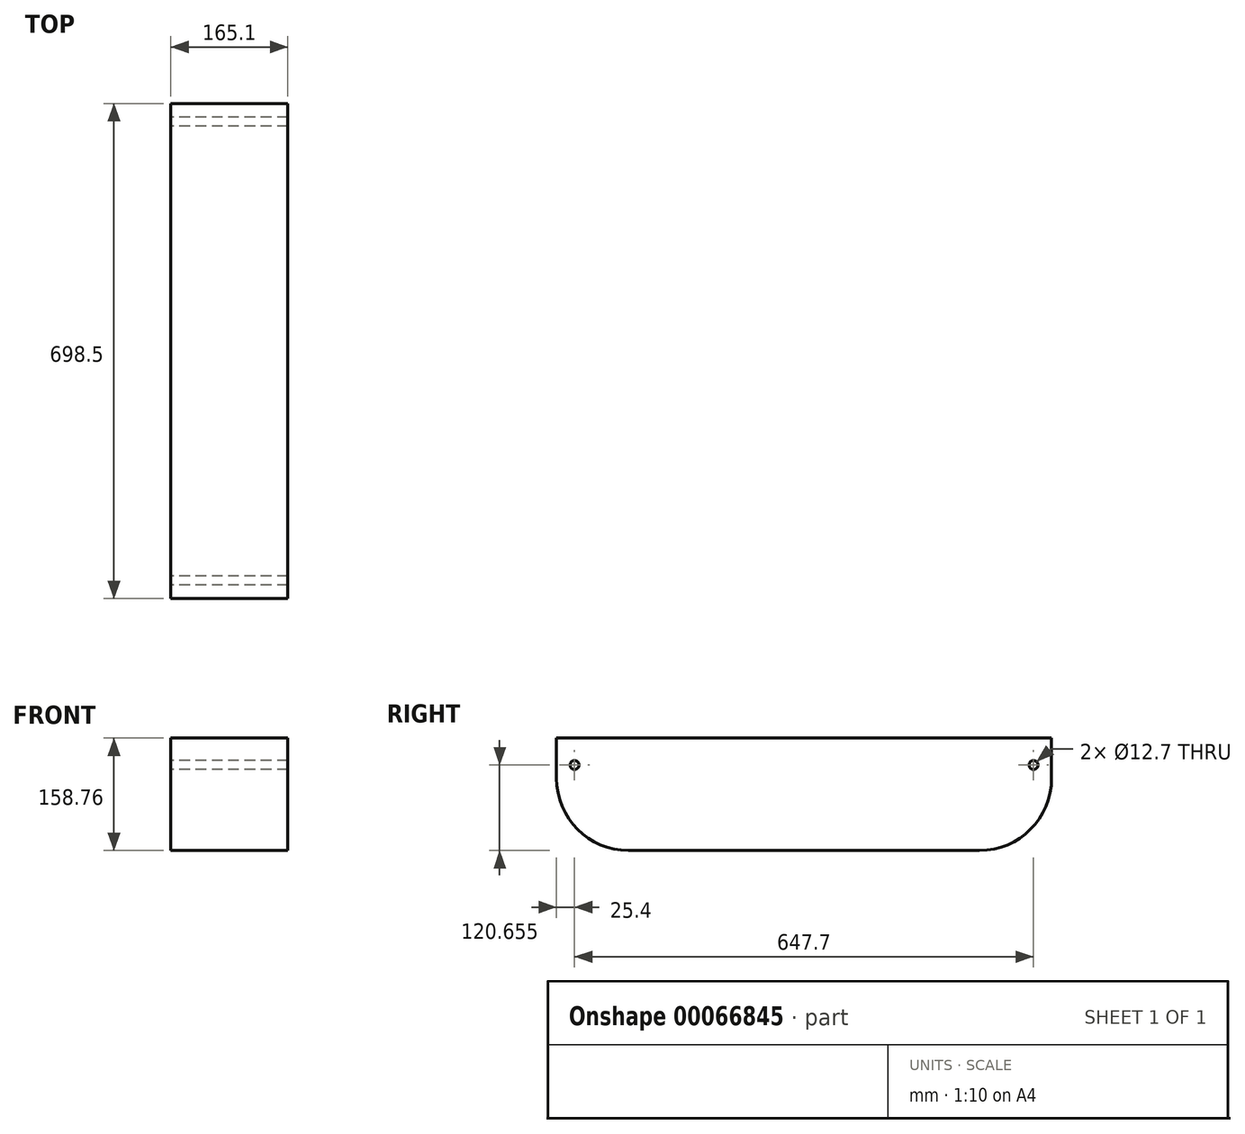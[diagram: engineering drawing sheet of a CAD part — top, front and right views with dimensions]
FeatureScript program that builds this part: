
annotation { "Feature Type Name" : "Feature", "Feature Type Description" : "" }
export const myFeature = defineFeature(function(context is Context, id is Id, definition is map)
    precondition{}
    {
        {
            var Q0;
            Q0=qCreatedBy(makeId("Right.planeOp"),FACE);
            var sketch = newSketch(context, id + "F0", { "sketchPlane" : qUnion([Q0])});
            skLineSegment(sketch, "E0.rect.bottom", {"start": v(349.25, 79.38) * mm, "end": v(-349.25, 79.38) * mm});
            skLineSegment(sketch, "E0.rect.top", {"start": v(349.25, -79.37) * mm, "end": v(-349.25, -79.37) * mm});
            skLineSegment(sketch, "E0.rect.left", {"start": v(349.25, 79.38) * mm, "end": v(349.25, -79.37) * mm});
            skLineSegment(sketch, "E0.rect.right", {"start": v(-349.25, 79.38) * mm, "end": v(-349.25, -79.37) * mm});
            skPoint(sketch, "E0.rect.middle", {"position": v(0, 0) * mm});
            skCircle(sketch, "E1", {"center": v(323.85, 41.27) * mm, "radius": 6.35 * mm});
            skCircle(sketch, "E2", {"center": v(-323.85, 41.27) * mm, "radius": 6.35 * mm});
            skSolve(sketch);
        }
        {
            var Q0;
            Q0=makeQuery(id+"F0.imprint","IMPRINT",FACE,{"disambiguationData":[TD([[makeQuery(id+"F0.imprint","IMPRINT",EDGE,{"derivedFrom":sQuery(id+"F0.wireOp",EDGE,"E0.rect.bottom")}),1.0]])]});
            extrude(context, id + "F1", {"entities" : qUnion([Q0]), "depth" : 165.1 * mm});
        }
        {
            var Q0;
            Q0=makeQuery(id+"F1.opExtrude","SWEPT_EDGE",EDGE,{"disambiguationData":[OSD([sQuery(id+"F0.wireOp",EDGE,"E0.rect.top"),sQuery(id+"F0.wireOp",EDGE,"E0.rect.left")])]});
            fillet(context, id + "F2", {"entities" : qUnion([Q0]), "radius" : 101.6 * mm, "tangentPropagation" : true, "allowEdgeOverflow" : false});
        }
        {
            var Q0;
            Q0=makeQuery(id+"F1.opExtrude","SWEPT_EDGE",EDGE,{"disambiguationData":[OSD([sQuery(id+"F0.wireOp",EDGE,"E0.rect.top"),sQuery(id+"F0.wireOp",EDGE,"E0.rect.right")])]});
            fillet(context, id + "F3", {"entities" : qUnion([Q0]), "radius" : 101.6 * mm, "tangentPropagation" : true, "allowEdgeOverflow" : false});
        }
    });
